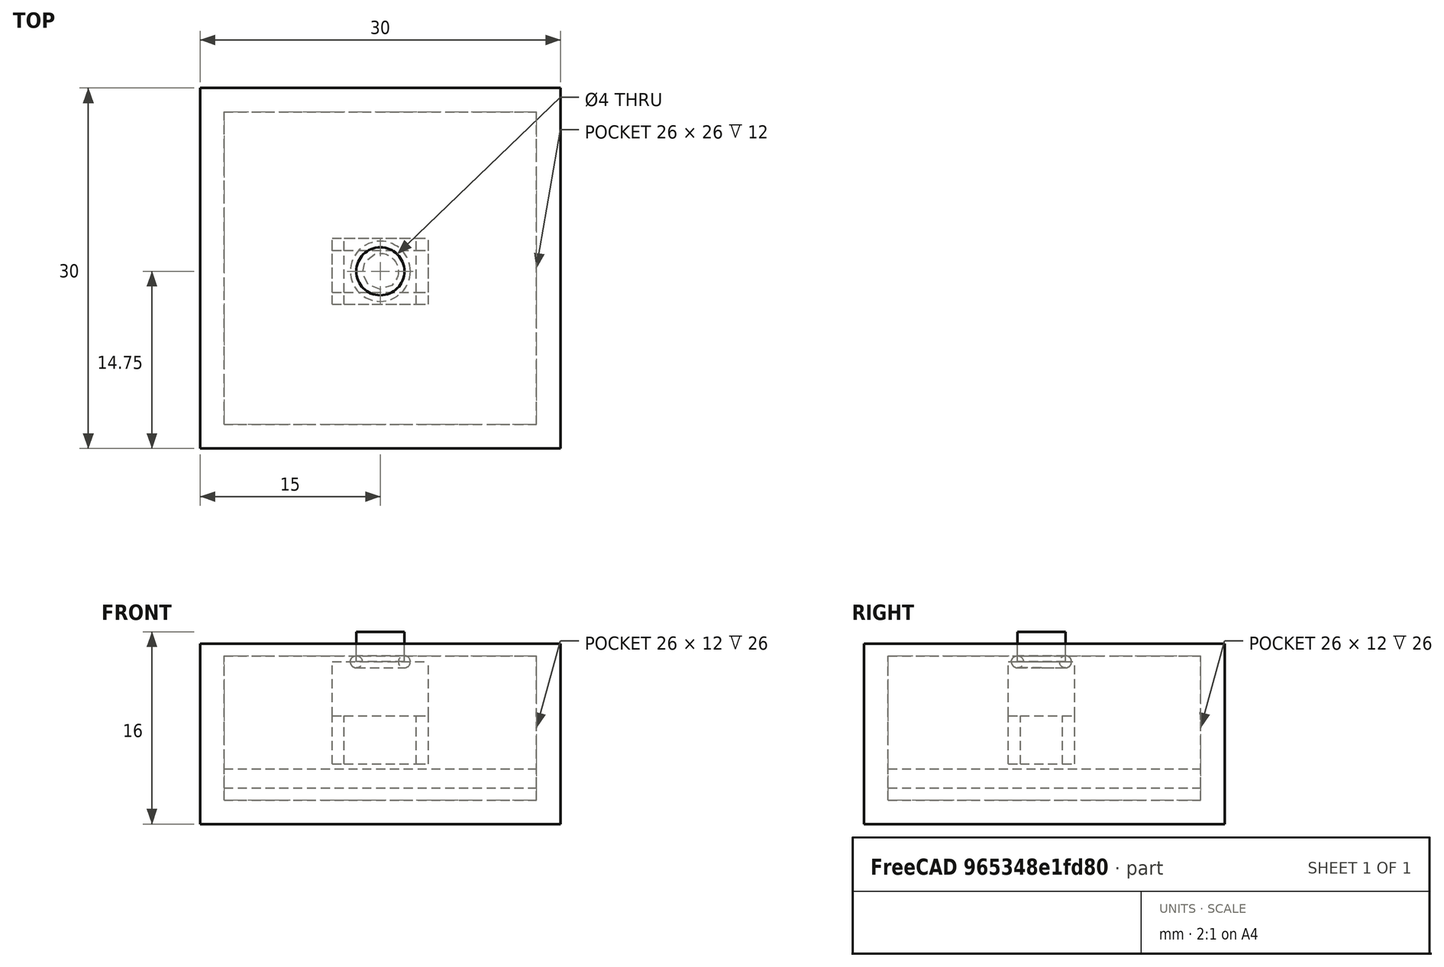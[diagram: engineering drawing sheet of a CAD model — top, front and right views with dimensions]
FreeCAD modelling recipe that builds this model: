
FCSTD DOCUMENT  (FreeCAD 0.15R4671 (Git))
Label: Button_V02
License: All rights reserved
LicenseURL: http://en.wikipedia.org/wiki/All_rights_reserved
objects: Part::Box×8, Mesh::Feature×2, Part::Cut×2, Part::Cylinder×2, Part::Torus×1, Part::MultiFuse×1
note: 14 computed .brp shape members not serialized (recipe doc carries the construction recipe); baked Part::Feature solids carry a one-line shape summary decoded from their .brp

FEATURE [Part::Box] Box  label="PCB"
  Height = 1.6
  Length = 26
  Placement = pos=(2,2,3) rot=(0,0,1;0rad)
  Width = 26
FEATURE [Mesh::Feature] Button_TC_1101T_C_A_B  label="Button_TC-1101T-C-A-B001"
  Placement = pos=(12,19,4.6) rot=(0,0,1;0rad)
FEATURE [Mesh::Feature] Button_TC_1101T_C_A_B001  label="Button_TC-1101T-C-A-B"
  Placement = pos=(12,13,4.6) rot=(0,0,1;0rad)
FEATURE [Part::Box] Box001  label="Box_out"
  Height = 15
  Length = 30
  Width = 30
FEATURE [Part::Box] Box002  label="Box_in"
  Height = 12
  Length = 26
  Placement = pos=(2,2,2) rot=(0,0,1;0rad)
  Width = 26
FEATURE [Part::Cut] Cut
  Base = -> Box001
  Tool = -> Box002
FEATURE [Part::Box] Box003  label="Cube"
  Height = 4.5
  Length = 8
  Placement = pos=(11,12,9) rot=(0,0,1;0rad)
  Width = 5.5
FEATURE [Part::Cylinder] Cylinder
  Angle = 360
  Height = 3
  Placement = pos=(15,14.75,13) rot=(0,0,1;0rad)
  Radius = 2
FEATURE [Part::Cylinder] Cylinder001  label="Cylinder_cut"
  Angle = 360
  Height = 3
  Placement = pos=(15,14.75,13) rot=(0,0,1;0rad)
  Radius = 2
FEATURE [Part::Cut] Cut001
  Base = -> Cut
  Tool = -> Cylinder001
FEATURE [Part::Torus] Torus
  Angle1 = -180
  Angle2 = 180
  Angle3 = 360
  Placement = pos=(15,14.75,13.5) rot=(0,0,1;0rad)
  Radius1 = 2
  Radius2 = 0.5
FEATURE [Part::Box] Box004  label="Cube001"
  Height = 4
  Length = 1
  Placement = pos=(11,13,5) rot=(0,0,1;0rad)
  Width = 3.5
FEATURE [Part::Box] Box005  label="Cube002"
  Height = 4
  Length = 1
  Placement = pos=(18,13,5) rot=(0,0,1;0rad)
  Width = 3.5
FEATURE [Part::Box] Box006  label="Cube003"
  Height = 4
  Length = 6
  Placement = pos=(12,12,5) rot=(0,0,1;0rad)
  Width = 1
FEATURE [Part::Box] Box007  label="Cube004"
  Height = 4
  Length = 6
  Placement = pos=(12,16.5,5) rot=(0,0,1;0rad)
  Width = 1
FEATURE [Part::MultiFuse] Fusion  label="Bt_Ex001"
  Shapes = -> [Box003,Box004,Box005,Cylinder,Box006,Box007]
